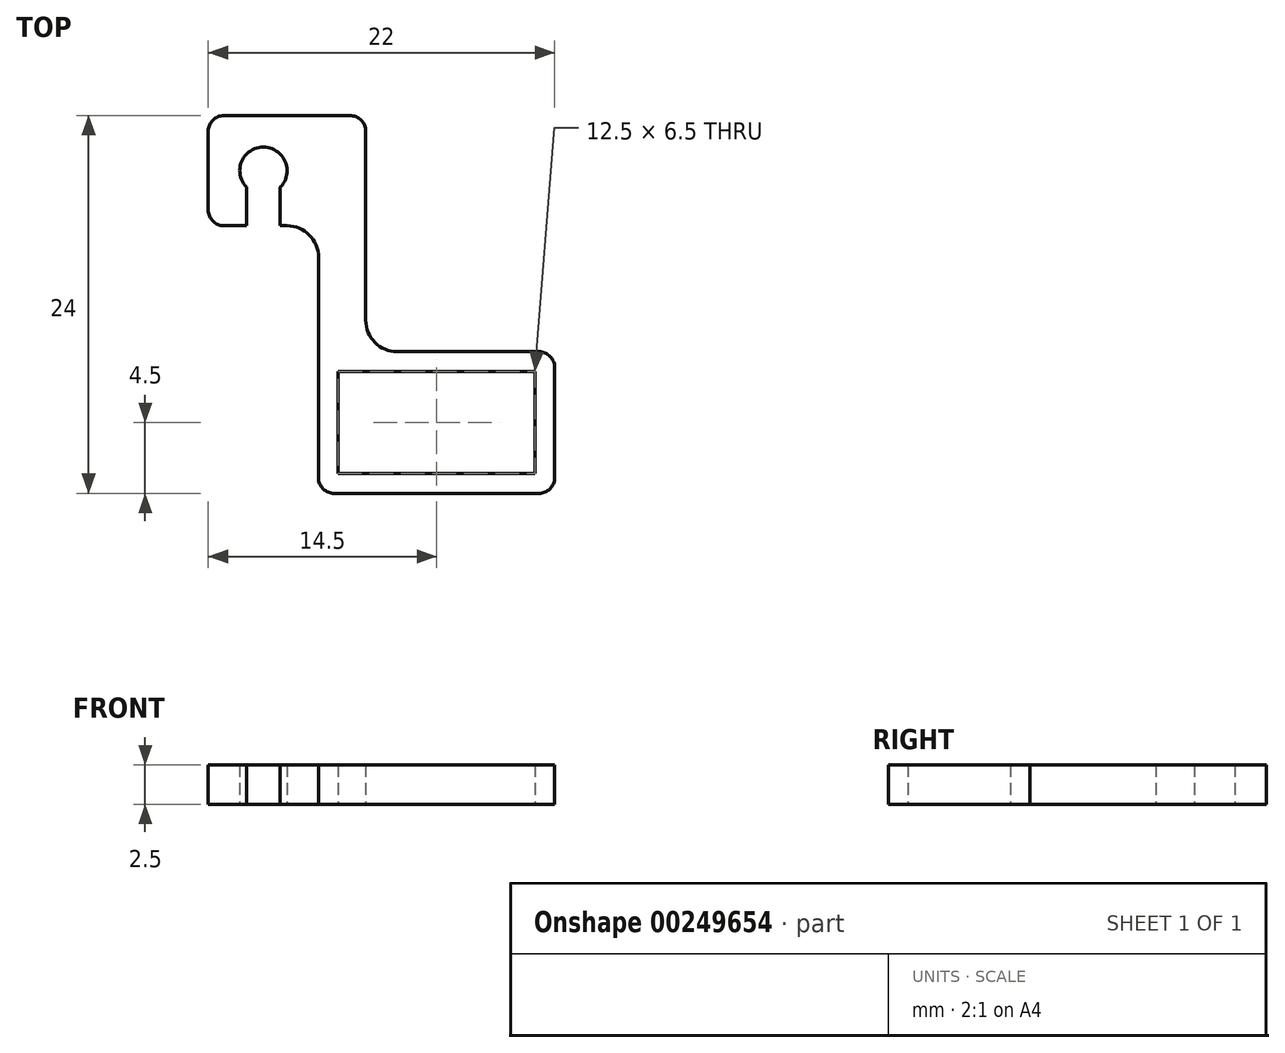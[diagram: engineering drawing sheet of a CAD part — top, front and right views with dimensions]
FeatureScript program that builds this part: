
annotation { "Feature Type Name" : "Feature", "Feature Type Description" : "" }
export const myFeature = defineFeature(function(context is Context, id is Id, definition is map)
    precondition{}
    {
        {
            var Q0;
            Q0=qCreatedBy(makeId("Top.planeOp"),FACE);
            var sketch = newSketch(context, id + "F0", { "sketchPlane" : qUnion([Q0])});
            skLineSegment(sketch, "E0.bottom", {"start": v(-6.25, 3.25) * mm, "end": v(6.25, 3.25) * mm});
            skLineSegment(sketch, "E0.top", {"start": v(-6.25, -3.25) * mm, "end": v(6.25, -3.25) * mm});
            skLineSegment(sketch, "E0.left", {"start": v(-6.25, 3.25) * mm, "end": v(-6.25, -3.25) * mm});
            skLineSegment(sketch, "E0.right", {"start": v(6.25, 3.25) * mm, "end": v(6.25, -3.25) * mm});
            skPoint(sketch, "E0.middle", {"position": v(0, 0) * mm});
            skLineSegment(sketch, "E1.bottom", {"start": v(-2.5, 4.5) * mm, "end": v(6.5, 4.5) * mm});
            skLineSegment(sketch, "E1.top", {"start": v(-6.5, -4.5) * mm, "end": v(6.5, -4.5) * mm});
            skLineSegment(sketch, "E1.left", {"start": v(-7.5, 4.5) * mm, "end": v(-7.5, -3.5) * mm});
            skLineSegment(sketch, "E1.right", {"start": v(7.5, 3.5) * mm, "end": v(7.5, -3.5) * mm});
            skLineSegment(sketch, "E2.top", {"start": v(-7.5, 19.5) * mm, "end": v(-5.5, 19.5) * mm});
            skLineSegment(sketch, "E2.left", {"start": v(-7.5, 4.5) * mm, "end": v(-7.5, 10.5) * mm});
            skLineSegment(sketch, "E2.right", {"start": v(-4.5, 6.5) * mm, "end": v(-4.5, 18.5) * mm});
            skLineSegment(sketch, "E3.bottom", {"start": v(-7.5, 19.5) * mm, "end": v(-13.5, 19.5) * mm});
            skLineSegment(sketch, "E3.top", {"start": v(-9.5, 12.5) * mm, "end": v(-9.93, 12.5) * mm});
            skLineSegment(sketch, "E3.right", {"start": v(-14.5, 18.5) * mm, "end": v(-14.5, 16) * mm});
            skPoint(sketch, "E4.centerSnap0", {"position": v(-14.5, 16) * mm});
            skLineSegment(sketch, "E5.trimOffspring", {"start": v(-14.5, 16) * mm, "end": v(-14.5, 13.5) * mm});
            skPoint(sketch, "E4.center.orphan", {"position": v(-11, 16) * mm});
            skArc(sketch, "E6", {"start": v(-9.93, 14.95) * mm, "mid": v(-11, 17.5) * mm, "end": v(-12.07, 14.95) * mm});
            skLineSegment(sketch, "E7", {"start": v(-12.07, 14.95) * mm, "end": v(-12.07, 12.5) * mm});
            skLineSegment(sketch, "E8", {"start": v(-9.93, 14.95) * mm, "end": v(-9.93, 12.5) * mm});
            skLineSegment(sketch, "E9.trimOffspring", {"start": v(-12.07, 12.5) * mm, "end": v(-13.5, 12.5) * mm});
            skPoint(sketch, "E10.visualSharp", {"position": v(-4.5, 4.5) * mm});
            skArc(sketch, "E10.filletArc", {"start": v(-4.5, 6.5) * mm, "mid": v(-3.91, 5.09) * mm, "end": v(-2.5, 4.5) * mm});
            skPoint(sketch, "E11.visualSharp", {"position": v(-7.5, 12.5) * mm});
            skArc(sketch, "E11.filletArc", {"start": v(-7.5, 10.5) * mm, "mid": v(-8.09, 11.91) * mm, "end": v(-9.5, 12.5) * mm});
            skPoint(sketch, "E12.visualSharp", {"position": v(-4.5, 19.5) * mm});
            skArc(sketch, "E12.filletArc", {"start": v(-4.5, 18.5) * mm, "mid": v(-4.8, 19.2) * mm, "end": v(-5.5, 19.5) * mm});
            skPoint(sketch, "E13.visualSharp", {"position": v(-14.5, 19.5) * mm});
            skArc(sketch, "E13.filletArc", {"start": v(-13.5, 19.5) * mm, "mid": v(-14.2, 19.2) * mm, "end": v(-14.5, 18.5) * mm});
            skPoint(sketch, "E14.visualSharp", {"position": v(-14.5, 12.5) * mm});
            skArc(sketch, "E14.filletArc", {"start": v(-14.5, 13.5) * mm, "mid": v(-14.2, 12.8) * mm, "end": v(-13.5, 12.5) * mm});
            skPoint(sketch, "E15.visualSharp", {"position": v(7.5, 4.5) * mm});
            skArc(sketch, "E15.filletArc", {"start": v(7.5, 3.5) * mm, "mid": v(7.2, 4.2) * mm, "end": v(6.5, 4.5) * mm});
            skPoint(sketch, "E16.visualSharp", {"position": v(7.5, -4.5) * mm});
            skArc(sketch, "E16.filletArc", {"start": v(6.5, -4.5) * mm, "mid": v(7.2, -4.2) * mm, "end": v(7.5, -3.5) * mm});
            skPoint(sketch, "E17.visualSharp", {"position": v(-7.5, -4.5) * mm});
            skArc(sketch, "E17.filletArc", {"start": v(-7.5, -3.5) * mm, "mid": v(-7.2, -4.2) * mm, "end": v(-6.5, -4.5) * mm});
            skSolve(sketch);
        }
        {
            var Q0;
            Q0=makeQuery(id+"F0.imprint","IMPRINT",FACE,{"disambiguationData":[TD([[makeQuery(id+"F0.imprint","IMPRINT",EDGE,{"derivedFrom":sQuery(id+"F0.wireOp",EDGE,"E0.bottom")}),1.0]])]});
            extrude(context, id + "F1", {"entities" : qUnion([Q0]), "depth" : 2.5 * mm});
        }
    });
